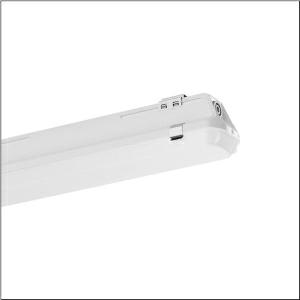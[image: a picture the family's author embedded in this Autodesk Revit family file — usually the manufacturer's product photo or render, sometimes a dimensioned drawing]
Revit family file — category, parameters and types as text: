
# Revit family: monsun_r__11_emergency_51fp107p467h3g_a613
name_source: partatom
category: Lighting Fixtures
units: mm (PartAtom-declared; Revit-internal decimal feet)

## family parameters
Cut with Voids When Loaded = No
Host = Face
Light Source = No
Part Type = Normal
Room Calculation Point = No
Round Connector Dimension = Use Diameter
Shared = No

## types (1)
- Monsun® 11 emergency (1 x LED, 6050 lm, 37.2 W, 4000K)
    Apparent Load = 37 VA
    CIE Flux Codes = 47 77 93 94 100
    Color Rendering = 80
    Color Temperature = 4000K
    Default Elevation = 1800 mm
    Description = Monsun® 11 emergency, damp-proof luminaire, chain hanger, primary optical cover: enclosure, of PMMA, light emission: direct distribution, primary light characteristic: symmetric, installation type: suspended mounting, surface-mounted, horizontal mounting, vertical mounting, LED, rated luminous flux: 6.050lm, luminous efficacy: 163lm/W, light colour: 840, colour temperature: 4000K, control gear: ECG, with terminal, 4-pole, max. 2.5mm², mains connection: 220..240V, AC, 50/60Hz, rated input power: 37W, control gear: single battery element, battery: NiCd, 4,5Ah, mains connection: 230V, 50Hz, luminaire housing, of glass-fibre reinforced polyester, uncoated, bright grey, incl. chain hanger, length: 1.590mm, width: 90mm, height: 88mm, clip for enclosure, of stainless steel (V2A), ceiling mounting element, of stainless steel (V2A), chain hanger, of stainless steel (V2A), protection rating (complete): IP66, insulation class (complete): insulation class I (protective earthing), certification: CE, UKCA, protection symbol: D, impact resistance: IK04, permissible operating ambient temperature: +5..+35°C, standard: EN 50419, EN 60598-2-1, EN 60598-2-22, no direct snow, no direct sun, no direct rain, for indoor or canopied outdoor use, corresponds to IFS (International Featured Standards) requirements for safety and quality in the food industry, contact your sales advisor before using the luminaires in applications with unclear chemical exposure, large temperature fluctuations or condensation-forming humidity, LABS conformity tested according to VDMA 24364:2018-05, packaging unit: 1 piece
    Height = 89 mm
    Lamp = 1 x LED
    Lamp Light Flux = 6050 lm
    Lamp Power = 37.2 W
    Lamp count = 1
    Length = 1590 mm
    Luminous efficacy = 163 lm/W
    Manufacturer = Siteco
    ModVariant = No
    Model = 51FP107P467H3G
    Mounting Place = Ceiling
    Mounting Type = Surface mounted
    Number of Poles = 1
    OnlyDefault = Yes
    Power Factor = 1
    Product Name = Monsun® 11 emergency
    Product group = damp-proof luminaire
    ProductGroupID = 300
    Protection Class = Protection class I
    Protection Degree = IP 66
    RLX_Detail_Level = 1
    RLX_Emergency_Light_Flux = 0 lm
    RLX_Emergency_Type = 0
    RLX_Emergency_Type_DB = No
    RlxData = <blob elided: 89421 chars, md5=d0d7b46e>
    Socket = socket
    Standby Power = 0 W
    System Light Flux = 6050 lm
    System Power = 37 W
    Type Comments = Product without accessories
    Type Image = l_1319650.jpg
    URL = http://relux.com
    VarID = ---
    Voltage = 0 V
    Weight = 0.00 kg
    Width = 90 mm

## geometry (parser evidence)
native form markers: Blend x4, Sweep x11
no freeform markers — native parametric forms only
